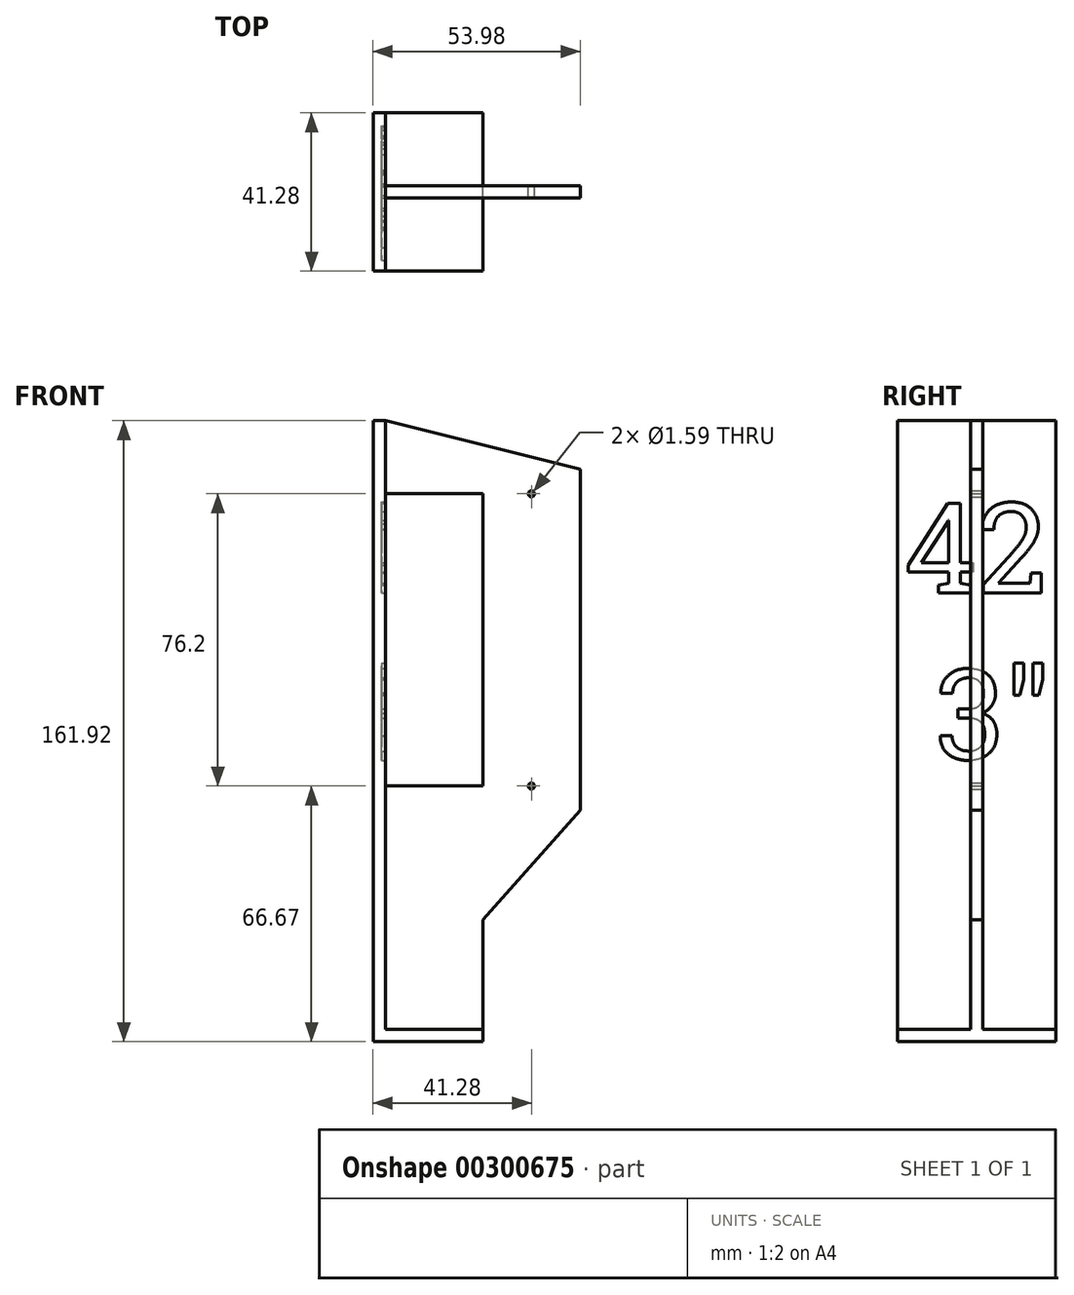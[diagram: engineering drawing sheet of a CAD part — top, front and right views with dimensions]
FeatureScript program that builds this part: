
annotation { "Feature Type Name" : "Feature", "Feature Type Description" : "" }
export const myFeature = defineFeature(function(context is Context, id is Id, definition is map)
    precondition{}
    {
        {
            var Q0;
            Q0=qCreatedBy(makeId("Front.planeOp"),FACE);
            var sketch = newSketch(context, id + "F0", { "sketchPlane" : qUnion([Q0])});
            skLineSegment(sketch, "E0", {"start": v(25.4, 28.57) * mm, "end": v(50.8, 57.15) * mm});
            skLineSegment(sketch, "E1", {"start": v(50.8, 57.15) * mm, "end": v(50.8, 146.05) * mm});
            skLineSegment(sketch, "E2", {"start": v(50.8, 146.05) * mm, "end": v(0, 158.75) * mm});
            skLineSegment(sketch, "E3", {"start": v(0, 158.75) * mm, "end": v(0, 139.7) * mm});
            skCircle(sketch, "E4", {"center": v(38.1, 63.5) * mm, "radius": 0.8 * mm});
            skCircle(sketch, "E5", {"center": v(38.1, 139.7) * mm, "radius": 0.8 * mm});
            skLineSegment(sketch, "E6.bottom", {"start": v(0, 63.5) * mm, "end": v(25.4, 63.5) * mm});
            skLineSegment(sketch, "E6.top", {"start": v(0, 139.7) * mm, "end": v(25.4, 139.7) * mm});
            skLineSegment(sketch, "E6.right", {"start": v(25.4, 63.5) * mm, "end": v(25.4, 139.7) * mm});
            skLineSegment(sketch, "E7.trimOffspring", {"start": v(0, 63.5) * mm, "end": v(0, 0) * mm});
            skLineSegment(sketch, "E8", {"start": v(25.4, 28.57) * mm, "end": v(25.4, 0) * mm});
            skLineSegment(sketch, "E9", {"start": v(25.4, 0) * mm, "end": v(0, 0) * mm});
            skSolve(sketch);
        }
        {
            var Q0;
            Q0 = qSketchRegion(id + "F0", true);
            extrude(context, id + "F1", {"entities" : qUnion([Q0]), "endBound" : BoundingType.SYMMETRIC, "depth" : 3.17 * mm});
        }
        {
            var Q0;
            Q0=qCreatedBy(makeId("Right.planeOp"),FACE);
            var sketch = newSketch(context, id + "F2", { "sketchPlane" : qUnion([Q0])});
            skLineSegment(sketch, "E10.bottom", {"start": v(20.64, 0) * mm, "end": v(-20.64, 0) * mm});
            skLineSegment(sketch, "E10.top", {"start": v(20.64, 158.75) * mm, "end": v(-20.64, 158.75) * mm});
            skLineSegment(sketch, "E10.left", {"start": v(20.64, 0) * mm, "end": v(20.64, 158.75) * mm});
            skLineSegment(sketch, "E10.right", {"start": v(-20.64, 0) * mm, "end": v(-20.64, 158.75) * mm});
            skSolve(sketch);
        }
        {
            var Q0;
            Q0 = qSketchRegion(id + "F2", true);
            extrude(context, id + "F3", {"entities" : qUnion([Q0]), "operationType" : NewBodyOperationType.ADD, "oppositeDirection" : true, "depth" : 3.17 * mm});
        }
        {
            var Q0;
            Q0=makeQuery(id+"F3.opExtrude","SWEPT_FACE",FACE,{"disambiguationData":[OSD([sQuery(id+"F2.wireOp",EDGE,"E10.bottom")])]});
            var sketch = newSketch(context, id + "F4", { "sketchPlane" : qUnion([Q0])});
            skLineSegment(sketch, "E11.bottom", {"start": v(-3.18, 20.64) * mm, "end": v(25.4, 20.64) * mm});
            skLineSegment(sketch, "E11.top", {"start": v(-3.18, -20.64) * mm, "end": v(25.4, -20.64) * mm});
            skLineSegment(sketch, "E11.left", {"start": v(-3.18, 20.64) * mm, "end": v(-3.18, -20.64) * mm});
            skLineSegment(sketch, "E11.right", {"start": v(25.4, 20.64) * mm, "end": v(25.4, -20.64) * mm});
            skSolve(sketch);
        }
        {
            var Q0;
            Q0 = qSketchRegion(id + "F4", true);
            extrude(context, id + "F5", {"entities" : qUnion([Q0]), "operationType" : NewBodyOperationType.ADD, "depth" : 3.17 * mm});
        }
        {
            var Q0;
            Q0=makeQuery(id+"F3.opExtrude","CAP_FACE",FACE,{"disambiguationData":[OSD([sQuery(id+"F2.wireOp",EDGE,"E10.bottom"),sQuery(id+"F2.wireOp",EDGE,"E10.top"),sQuery(id+"F2.wireOp",EDGE,"E10.left"),sQuery(id+"F2.wireOp",EDGE,"E10.right")])],"isStart":true});
            var sketch = newSketch(context, id + "F6", { "sketchPlane" : qUnion([Q0])});
            skText(sketch, "E12", { "text": "42\n 3\"", "fontName": "RobotoSlab-Regular.ttf"});
            const initialGuessF6  = {"E12": [-0.01884, 0.11387, 1, 0, 0.02366]};
            skSetInitialGuess(sketch, initialGuessF6);
            skSolve(sketch);
        }
        {
            var Q0;
            Q0 = qSketchRegion(id + "F6", true);
            extrude(context, id + "F7", {"entities" : qUnion([Q0]), "operationType" : NewBodyOperationType.REMOVE, "oppositeDirection" : true, "depth" : .9 * mm});
        }
    });
